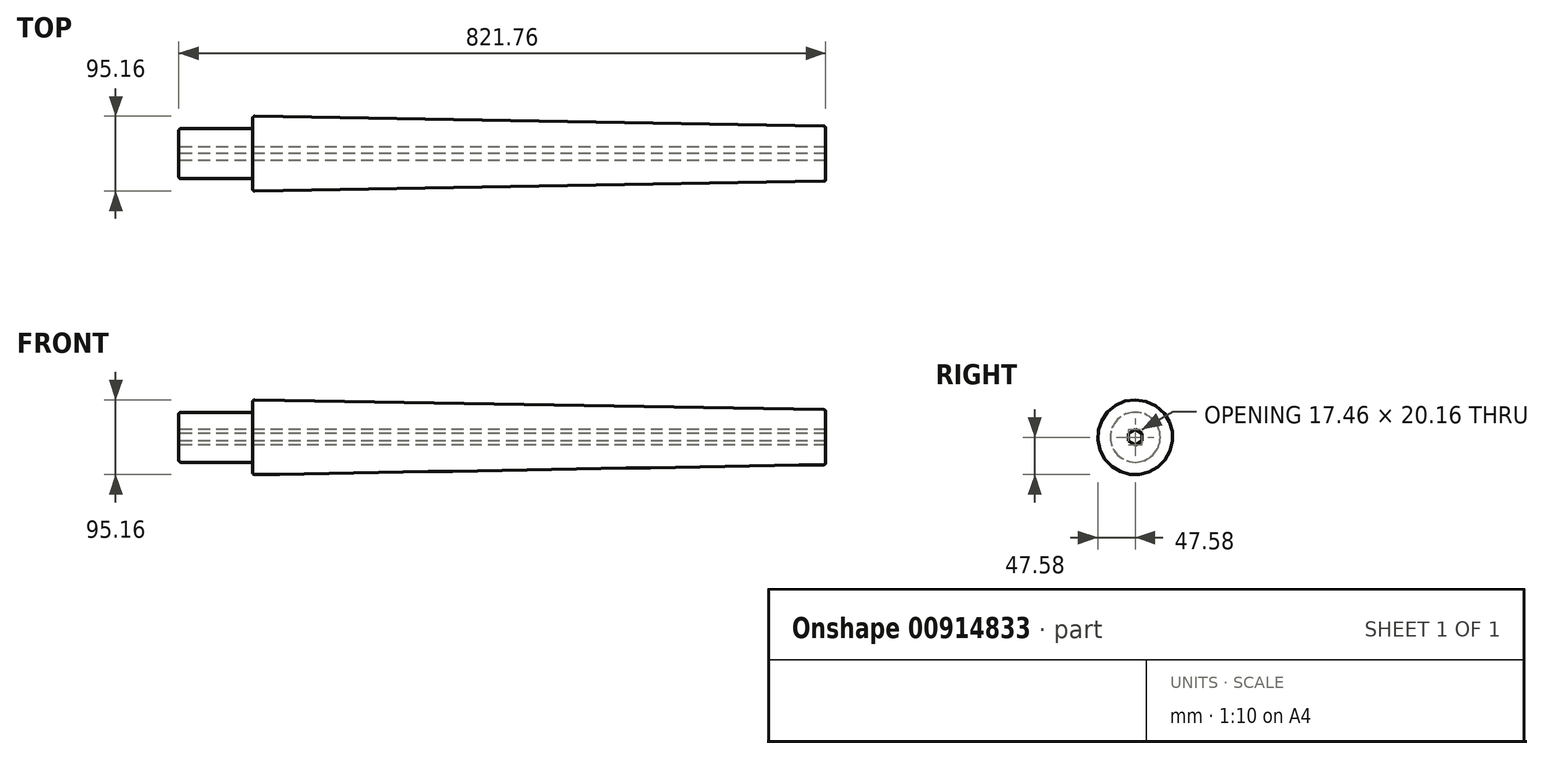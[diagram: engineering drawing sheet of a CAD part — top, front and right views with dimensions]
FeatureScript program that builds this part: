
annotation { "Feature Type Name" : "Feature", "Feature Type Description" : "" }
export const myFeature = defineFeature(function(context is Context, id is Id, definition is map)
    precondition{}
    {
        {
            var Q0;
            Q0=qCreatedBy(makeId("Front.planeOp"),FACE);
            var sketch = newSketch(context, id + "F0", { "sketchPlane" : qUnion([Q0])});
            skLineSegment(sketch, "E0", {"start": v(-410.88, 0) * mm, "end": v(410.88, 0) * mm});
            skLineSegment(sketch, "E1", {"start": v(-410.88, 31.75) * mm, "end": v(-410.88, 0) * mm});
            skLineSegment(sketch, "E2", {"start": v(410.88, 34.93) * mm, "end": v(410.88, 0) * mm});
            skLineSegment(sketch, "E3", {"start": v(-410.88, 31.75) * mm, "end": v(-317, 31.75) * mm});
            skLineSegment(sketch, "E4", {"start": v(-317, 31.75) * mm, "end": v(-317, 47.63) * mm});
            skLineSegment(sketch, "E5", {"start": v(-317, 47.63) * mm, "end": v(410.88, 34.93) * mm});
            skLineSegment(sketch, "E6", {"start": v(-351.14, 74.6) * mm, "end": v(-351.14, -85.58) * mm, "construction": true});
            skLineSegment(sketch, "E7", {"start": v(-386.07, 49.78) * mm, "end": v(-386.07, -85.58) * mm, "construction": true});
            skLineSegment(sketch, "E8", {"start": v(-386.07, 49.78) * mm, "end": v(-386.07, 0) * mm, "construction": true});
            skLineSegment(sketch, "E9", {"start": v(-351.14, 49.78) * mm, "end": v(-351.14, 0) * mm});
            skPoint(sketch, "E10.MirrorCS.end.orphan", {"position": v(-386.07, 0) * mm});
            skPoint(sketch, "E11.MirrorCS.end.orphan", {"position": v(-351.14, 0) * mm});
            skSolve(sketch);
        }
        {
            var Q0;
            Q0 = qSketchRegion(id + "F0", true);
            var Q1;
            Q1=sQuery(id+"F0.wireOp",EDGE,"E0");
            revolve(context, id + "F1", {"surfaceOperationType" : NewSurfaceOperationType.NEW, "entities" : qUnion([Q0]), "axis" : qUnion([Q1]), "revolveType" : RevolveType.FULL});
        }
        {
            var Q0;
            Q0=makeQuery(id+"F1.opRevolve","SWEPT_FACE",FACE,{"disambiguationData":[OSD([sQuery(id+"F0.wireOp",EDGE,"E1")])]});
            var sketch = newSketch(context, id + "F2", { "sketchPlane" : qUnion([Q0])});
            skCircle(sketch, "E12.cCircle", {"center": v(0, 0) * mm, "radius": 8.73 * mm, "construction": true});
            skLineSegment(sketch, "E12.0", {"start": v(-8.73, 5.04) * mm, "end": v(0, 10.08) * mm});
            skLineSegment(sketch, "E12.1", {"start": v(0, 10.08) * mm, "end": v(8.73, 5.04) * mm});
            skLineSegment(sketch, "E12.2", {"start": v(8.73, 5.04) * mm, "end": v(8.73, -5.04) * mm});
            skLineSegment(sketch, "E12.3", {"start": v(8.73, -5.04) * mm, "end": v(0, -10.08) * mm});
            skLineSegment(sketch, "E12.4", {"start": v(0, -10.08) * mm, "end": v(-8.73, -5.04) * mm});
            skLineSegment(sketch, "E12.5", {"start": v(-8.73, -5.04) * mm, "end": v(-8.73, 5.04) * mm});
            skPoint(sketch, "E12.0.midPoint", {"position": v(-4.37, 7.56) * mm});
            skSolve(sketch);
        }
        {
            var Q0;
            Q0=makeQuery(id+"F2.imprint","IMPRINT",FACE,{"disambiguationData":[TD([[makeQuery(id+"F2.imprint","IMPRINT",EDGE,{"derivedFrom":sQuery(id+"F2.wireOp",EDGE,"E12.0")}),-1.0]])]});
            extrude(context, id + "F3", {"entities" : qUnion([Q0]), "operationType" : NewBodyOperationType.REMOVE, "endBound" : BoundingType.THROUGH_ALL, "oppositeDirection" : true, "depth" : 25.4 * mm, "offsetDistance" : 25.4 * mm});
        }
        {
            var Q0;
            Q0=makeQuery(id+"F1.opRevolve","SWEPT_EDGE",EDGE,{"disambiguationData":[OSD([sQuery(id+"F0.wireOp",EDGE,"E4"),sQuery(id+"F0.wireOp",EDGE,"E5")])]});
            var Q1;
            Q1=makeQuery(id+"F1.opRevolve","SWEPT_EDGE",EDGE,{"disambiguationData":[OSD([sQuery(id+"F0.wireOp",EDGE,"E1"),sQuery(id+"F0.wireOp",EDGE,"E3")])]});
            var Q2;
            Q2=makeQuery(id+"F1.opRevolve","SWEPT_EDGE",EDGE,{"disambiguationData":[OSD([sQuery(id+"F0.wireOp",EDGE,"E5"),sQuery(id+"F0.wireOp",EDGE,"E2")])]});
            var Q3;
            Q3=makeQuery(id+"F1.opRevolve","SWEPT_EDGE",EDGE,{"disambiguationData":[OSD([sQuery(id+"F0.wireOp",EDGE,"E3"),sQuery(id+"F0.wireOp",EDGE,"E4")])]});
            fillet(context, id + "F4", {"entities" : qUnion([Q0, Q1, Q2, Q3]), "radius" : 2.54 * mm, "tangentPropagation" : true, "allowEdgeOverflow" : false});
        }
    });
